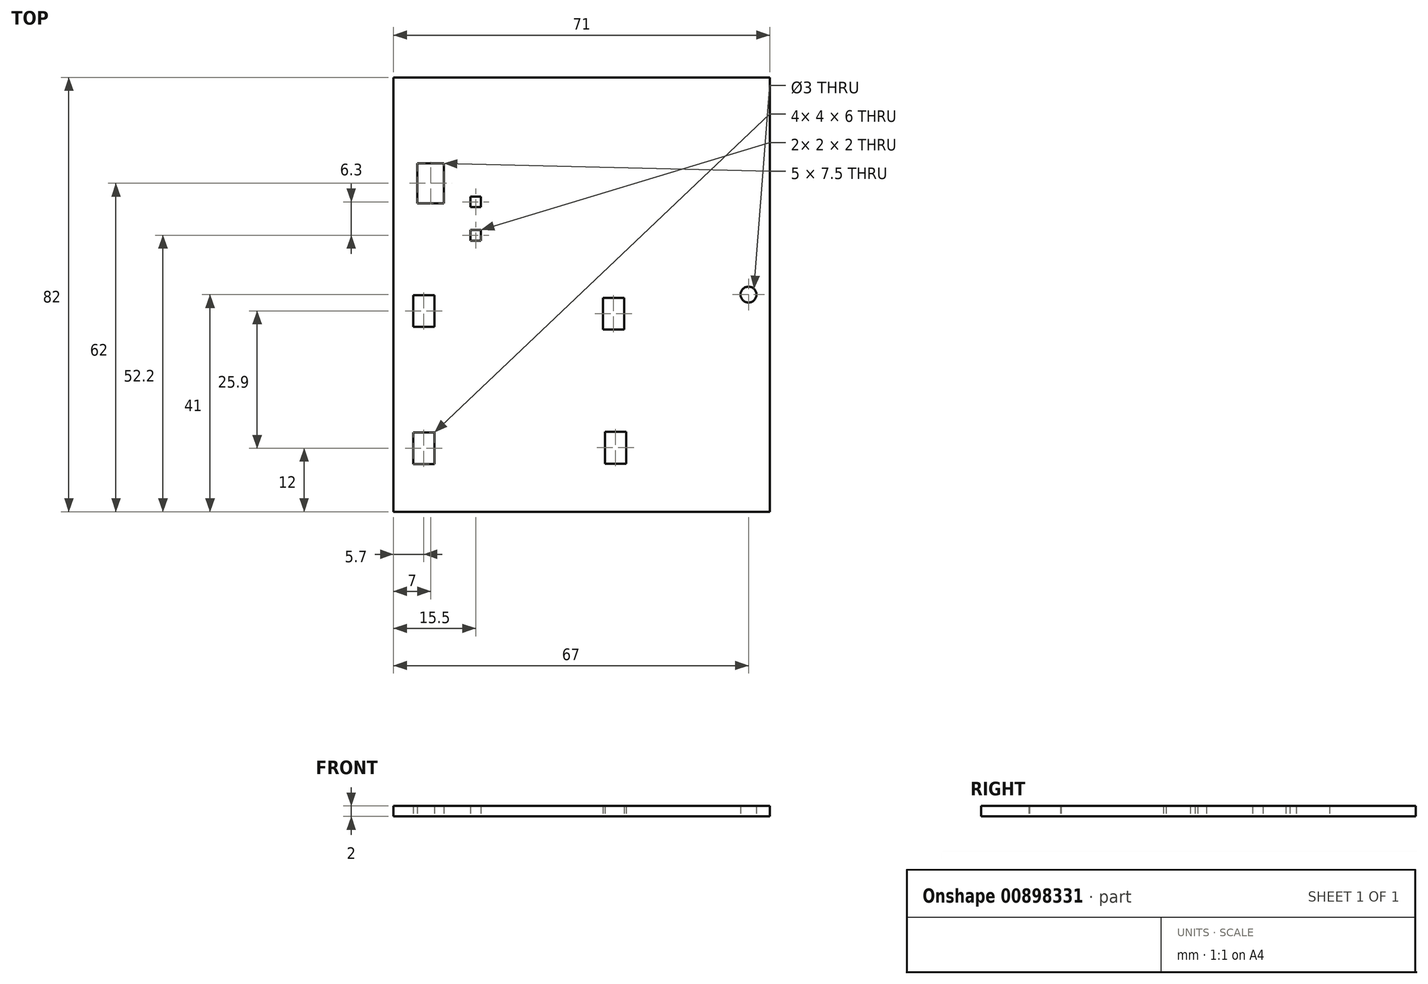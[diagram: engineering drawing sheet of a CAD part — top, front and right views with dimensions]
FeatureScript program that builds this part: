
annotation { "Feature Type Name" : "Feature", "Feature Type Description" : "" }
export const myFeature = defineFeature(function(context is Context, id is Id, definition is map)
    precondition{}
    {
        {
            var Q0;
            Q0=qCreatedBy(makeId("Top.planeOp"),FACE);
            var sketch = newSketch(context, id + "F0", { "sketchPlane" : qUnion([Q0])});
            skLineSegment(sketch, "E0.bottom", {"start": v(-35.5, 41) * mm, "end": v(35.5, 41) * mm});
            skLineSegment(sketch, "E0.top", {"start": v(-35.5, -41) * mm, "end": v(35.5, -41) * mm});
            skLineSegment(sketch, "E0.left", {"start": v(-35.5, 41) * mm, "end": v(-35.5, -41) * mm});
            skLineSegment(sketch, "E0.right", {"start": v(35.5, 41) * mm, "end": v(35.5, -41) * mm});
            skPoint(sketch, "E0.middle", {"position": v(0, 0) * mm});
            skCircle(sketch, "E1", {"center": v(31.5, 0) * mm, "radius": 1.5 * mm});
            skLineSegment(sketch, "E2.bottom", {"start": v(-31, 24.75) * mm, "end": v(-26, 24.75) * mm});
            skLineSegment(sketch, "E2.top", {"start": v(-31, 17.25) * mm, "end": v(-26, 17.25) * mm});
            skLineSegment(sketch, "E2.left", {"start": v(-31, 24.75) * mm, "end": v(-31, 17.25) * mm});
            skLineSegment(sketch, "E2.right", {"start": v(-26, 24.75) * mm, "end": v(-26, 17.25) * mm});
            skPoint(sketch, "E2.middle", {"position": v(-28.5, 21) * mm});
            skLineSegment(sketch, "E3.bottom", {"start": v(-31.8, -26) * mm, "end": v(-27.8, -26) * mm});
            skLineSegment(sketch, "E3.top", {"start": v(-31.8, -32) * mm, "end": v(-27.8, -32) * mm});
            skLineSegment(sketch, "E3.left", {"start": v(-31.8, -26) * mm, "end": v(-31.8, -32) * mm});
            skLineSegment(sketch, "E3.right", {"start": v(-27.8, -26) * mm, "end": v(-27.8, -32) * mm});
            skPoint(sketch, "E3.middle", {"position": v(-29.8, -29) * mm});
            skLineSegment(sketch, "E4.bottom", {"start": v(-31.8, -0.1) * mm, "end": v(-27.8, -0.1) * mm});
            skLineSegment(sketch, "E4.top", {"start": v(-31.8, -6.1) * mm, "end": v(-27.8, -6.1) * mm});
            skLineSegment(sketch, "E4.left", {"start": v(-31.8, -0.1) * mm, "end": v(-31.8, -6.1) * mm});
            skLineSegment(sketch, "E4.right", {"start": v(-27.8, -0.1) * mm, "end": v(-27.8, -6.1) * mm});
            skPoint(sketch, "E4.middle", {"position": v(-29.8, -3.1) * mm});
            skLineSegment(sketch, "E5.bottom", {"start": v(4.4, -25.9) * mm, "end": v(8.4, -25.9) * mm});
            skLineSegment(sketch, "E5.top", {"start": v(4.4, -31.9) * mm, "end": v(8.4, -31.9) * mm});
            skLineSegment(sketch, "E5.left", {"start": v(4.4, -25.9) * mm, "end": v(4.4, -31.9) * mm});
            skLineSegment(sketch, "E5.right", {"start": v(8.4, -25.9) * mm, "end": v(8.4, -31.9) * mm});
            skPoint(sketch, "E5.middle", {"position": v(6.4, -28.9) * mm});
            skLineSegment(sketch, "E6.bottom", {"start": v(4, -0.6) * mm, "end": v(8, -0.6) * mm});
            skLineSegment(sketch, "E6.top", {"start": v(4, -6.6) * mm, "end": v(8, -6.6) * mm});
            skLineSegment(sketch, "E6.left", {"start": v(4, -0.6) * mm, "end": v(4, -6.6) * mm});
            skLineSegment(sketch, "E6.right", {"start": v(8, -0.6) * mm, "end": v(8, -6.6) * mm});
            skPoint(sketch, "E6.middle", {"position": v(6, -3.6) * mm});
            skLineSegment(sketch, "E7.bottom", {"start": v(-21, 18.5) * mm, "end": v(-19, 18.5) * mm});
            skLineSegment(sketch, "E7.top", {"start": v(-21, 16.5) * mm, "end": v(-19, 16.5) * mm});
            skLineSegment(sketch, "E7.left", {"start": v(-21, 18.5) * mm, "end": v(-21, 16.5) * mm});
            skLineSegment(sketch, "E7.right", {"start": v(-19, 18.5) * mm, "end": v(-19, 16.5) * mm});
            skPoint(sketch, "E7.middle", {"position": v(-20, 17.5) * mm});
            skLineSegment(sketch, "E8.bottom", {"start": v(-19, 10.2) * mm, "end": v(-21, 10.2) * mm});
            skLineSegment(sketch, "E8.top", {"start": v(-19, 12.2) * mm, "end": v(-21, 12.2) * mm});
            skLineSegment(sketch, "E8.left", {"start": v(-19, 10.2) * mm, "end": v(-19, 12.2) * mm});
            skLineSegment(sketch, "E8.right", {"start": v(-21, 10.2) * mm, "end": v(-21, 12.2) * mm});
            skPoint(sketch, "E8.middle", {"position": v(-20, 11.2) * mm});
            skSolve(sketch);
        }
        {
            var Q0;
            Q0=makeQuery(id+"F0.imprint","IMPRINT",FACE,{"disambiguationData":[TD([[makeQuery(id+"F0.imprint","IMPRINT",EDGE,{"derivedFrom":sQuery(id+"F0.wireOp",EDGE,"E0.bottom")}),-1.0]])]});
            extrude(context, id + "F1", {"entities" : qUnion([Q0]), "depth" : 2 * mm, "offsetDistance" : 25 * mm});
        }
    });
